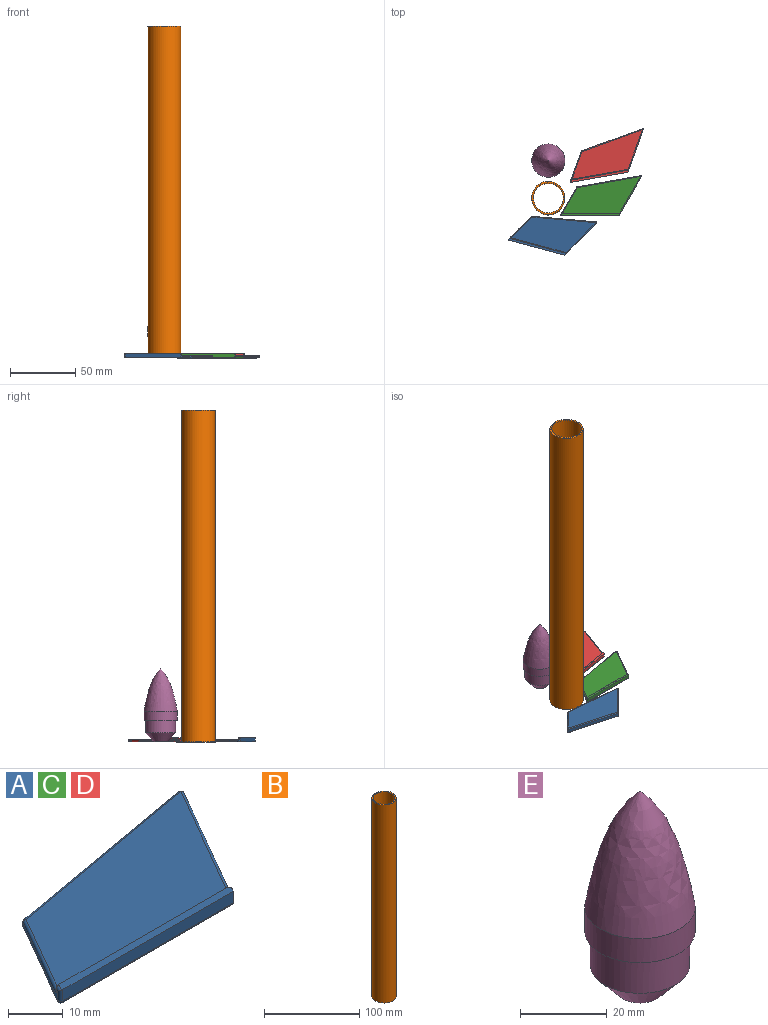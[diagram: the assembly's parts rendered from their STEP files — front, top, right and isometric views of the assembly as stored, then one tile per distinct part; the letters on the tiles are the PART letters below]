
ASSEMBLY  parts=5 mates=4
PART A: 29 faces, bbox 62.1x30.8x3.2 mm
  f0: plane 21.08x12.17mm, normal (-0.87,0.5,0), area 17.7mm2, adj f8,f12,f13,f16,f19,f20,f23
  f1: plane 29.93x17.28mm, normal (0.87,-0.5,0), area 25.6mm2, adj f3,f4,f15,f22,f26,f27,f28
  f2: plane 48.46x8.55mm, normal (-0.17,0.98,0), area 33.7mm2, adj f13,f14,f21,f22
  f3: plane 43.88x2.57mm, normal (0,-1,0), area 112.6mm2, adj f1,f4,f11,f12
  f4: plane 44.68x1.64mm, normal (0,0,1), area 72.2mm2, adj f1,f3,f6,f12,f16,f28
  f5: plane 60.63x29.62mm, normal (0,0,-1), area 1103.4mm2, adj f8,f11,f14,f15
  f6: plane 43.53x0.67mm, normal (0,1,0), area 28.7mm2, adj f4,f16,f19,f25,f28
  f7: plane 59.68x27.98mm, normal (0,0,1), area 1032.1mm2, adj f20,f21,f25,f26
  f8: cylinder r=0.61mm len=21.38mm, axis (-0.5,-0.87,0), area 23.3mm2, adj f0,f5,f9,f10
  f9: sphere r=0.61mm, area 0.8mm2, adj f8,f11,f12
  f10: sphere r=0.61mm, area 0.3mm2, adj f8,f13,f14
  f11: cylinder r=0.61mm len=43.88mm, axis (1,0,0), area 41.9mm2, adj f3,f5,f9,f15
  f12: cylinder r=0.61mm len=2.57mm, axis (0,0,-1), area 3.1mm2, adj f0,f3,f4,f9,f16
  f13: cylinder r=0.61mm len=0.69mm, axis (0,0,-1), area 0.4mm2, adj f0,f2,f10,f17
  f14: cylinder r=0.61mm len=48.57mm, axis (-0.98,-0.17,0), area 47.1mm2, adj f2,f5,f10,f18
  f15: cylinder r=0.61mm len=30.23mm, axis (0.5,0.87,0), area 33mm2, adj f1,f5,f11,f18
  f16: cylinder r=0.61mm len=1.86mm, axis (0.5,0.87,0), area 1.2mm2, adj f0,f4,f6,f12,f19
  f17: sphere r=0.61mm, area 0.3mm2, adj f13,f20,f21
  f18: sphere r=0.61mm, area 0.8mm2, adj f14,f15,f22
  f19: cylinder r=0.61mm len=0.58mm, axis (0,0,-1), area 0.2mm2, adj f0,f6,f16,f23
  f20: cylinder r=0.61mm len=19.74mm, axis (0.5,0.87,0), area 21.5mm2, adj f0,f7,f17,f23
  f21: cylinder r=0.61mm len=48.57mm, axis (0.98,0.17,0), area 47.1mm2, adj f2,f7,f17,f24
  f22: cylinder r=0.61mm len=0.91mm, axis (0,0,-1), area 0.9mm2, adj f1,f2,f18,f24
  f23: bspline ~1.43x1.35mm, area 1.2mm2, adj f0,f19,f20,f25
  f24: sphere r=0.61mm, area 0.8mm2, adj f21,f22,f26
  f25: cylinder r=0.61mm len=44.23mm, axis (1,0,0), area 41.7mm2, adj f6,f7,f23,f27
  f26: cylinder r=0.61mm len=28.29mm, axis (-0.5,-0.87,0), area 30.9mm2, adj f1,f7,f24,f27
  f27: bspline ~1.63x1.43mm, area 1.6mm2, adj f1,f25,f26,f28
  f28: cylinder r=0.61mm len=0.91mm, axis (0,0,-1), area 0.8mm2, adj f1,f4,f6,f27
PART B: 4 faces, bbox 25.4x25.4x254 mm
  f0: cylinder r=11.43mm len=254mm, axis (0,0,-1), area 18241.5mm2, adj f2,f3
  f1: cylinder r=12.7mm len=254mm, axis (0,0,-1), area 20268.3mm2, adj f2,f3
  f2: plane 25.4x25.4mm, normal (0,0,1), area 96.3mm2, adj f0,f1
  f3: plane 25.4x25.4mm, normal (0,0,-1), area 96.3mm2, adj f0,f1
PART C: same geometry as A
PART D: same geometry as A
PART E: 7 faces, bbox 25.4x25.4x55.9 mm
  f0: plane 10.72x10.72mm, normal (0,0,-1), area 90.2mm2, adj f3
  f1: plane 25.4x25.4mm, normal (0,0,-1), area 96.3mm2, adj f2,f4
  f2: cylinder r=11.43mm len=22.86mm, axis (0,0,-1), area 683.7mm2, adj f1,f3
  f3: cone r=11.43mm half-angle=40.9deg, axis (0,0,1), area 489.1mm2, adj f0,f2
  f4: cylinder r=12.7mm len=25.4mm, axis (0,0,-1), area 543.4mm2, adj f1,f5
  f5: revolved ~32.54x25.4mm, area 1785.9mm2, adj f4,f6
  f6: plane 0.34x0.34mm, normal (0,0,1), area 0.1mm2, adj f5
PLACE A rot(axis=(0,0,-1),15deg) t=(-0.48,-25.11,-25.09)mm
PLACE B t=(30.43,6.68,-25.09)mm
PLACE C t=(39.39,-6.73,-25.09)mm
PLACE D rot(axis=(0,0,1),10deg) t=(46.95,18.88,-25.09)mm
PLACE E t=(30.43,35.63,-25.09)mm
MATE parallel C.f5 <-> B.f1  axis (0,0,-1) through (70.82,6.68,-25.09)mm
MATE parallel D.f5 <-> B.f1  axis (0,0,-1) through (75.57,37.54,-25.09)mm
MATE parallel E.f2 <-> B.f1  axis (0,0,-1) through (30.43,35.63,-25.09)mm
MATE parallel A.f5 <-> B.f1  axis (0,0,-1) through (33.35,-20.29,-25.09)mm
